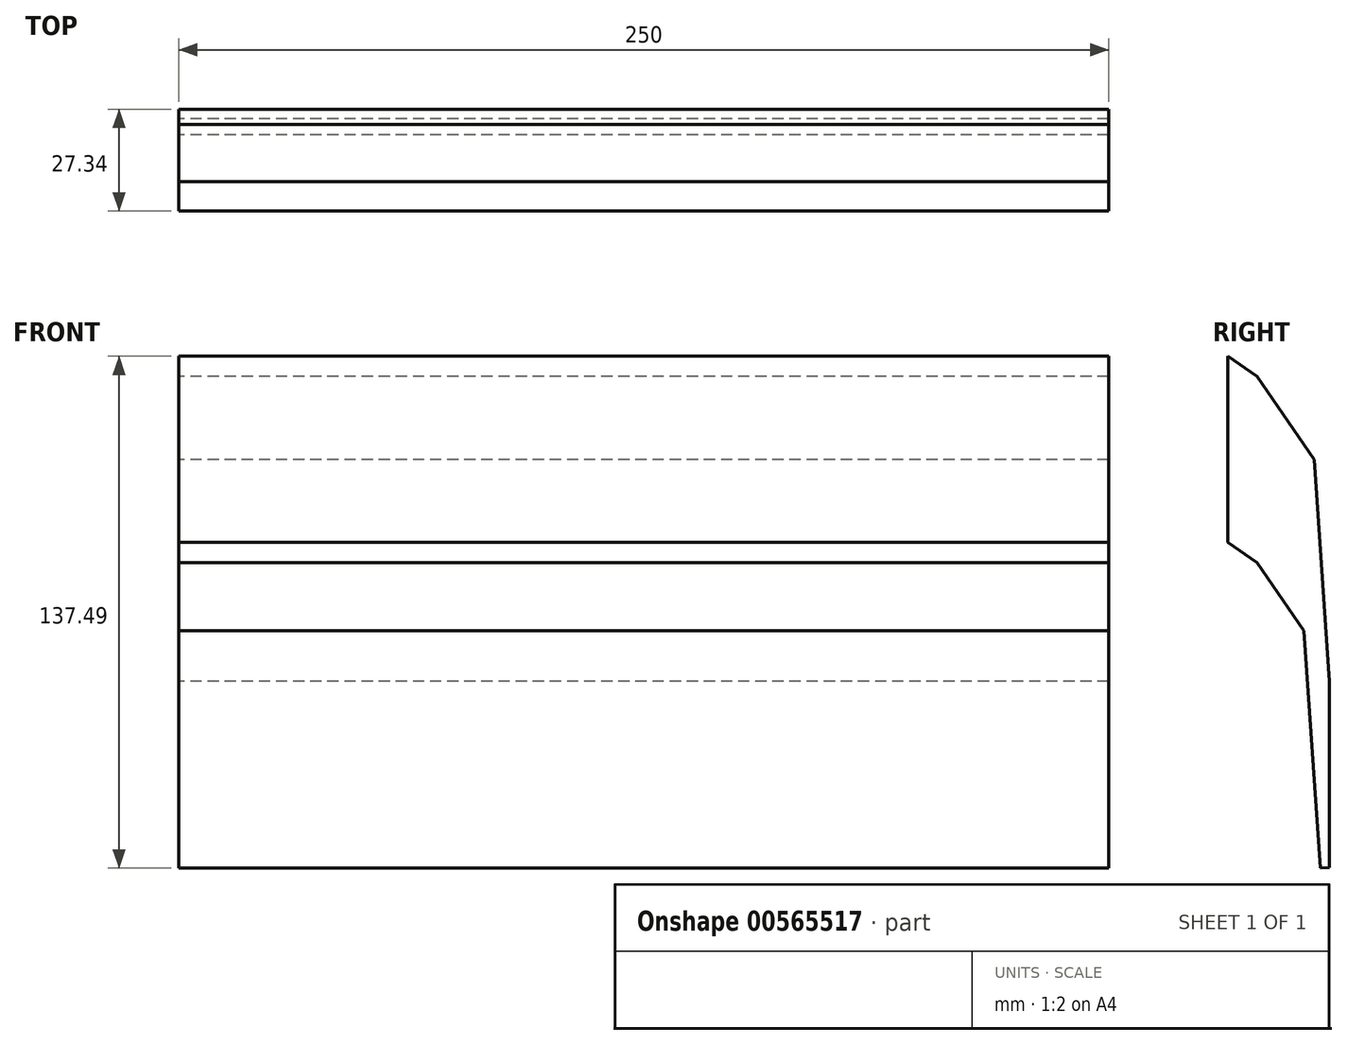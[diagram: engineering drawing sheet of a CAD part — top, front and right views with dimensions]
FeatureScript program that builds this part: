
annotation { "Feature Type Name" : "Feature", "Feature Type Description" : "" }
export const myFeature = defineFeature(function(context is Context, id is Id, definition is map)
    precondition{}
    {
        {
            var Q0;
            Q0=qCreatedBy(makeId("Front.planeOp"),FACE);
            var sketch = newSketch(context, id + "F0", { "sketchPlane" : qUnion([Q0])});
            skLineSegment(sketch, "E0.bottom", {"start": v(0, 0) * mm, "end": v(-250, 0) * mm});
            skLineSegment(sketch, "E0.top", {"start": v(0, 50) * mm, "end": v(-250, 50) * mm});
            skLineSegment(sketch, "E0.left", {"start": v(0, 0) * mm, "end": v(0, 50) * mm});
            skLineSegment(sketch, "E0.right", {"start": v(-250, 0) * mm, "end": v(-250, 50) * mm});
            skSolve(sketch);
        }
        {
            var Q0;
            Q0=qCreatedBy(makeId("Right.planeOp"),FACE);
            var sketch = newSketch(context, id + "F1", { "sketchPlane" : qUnion([Q0])});
            skLineSegment(sketch, "E1", {"start": v(0, 27.75) * mm, "end": v(-7.87, 22.34) * mm});
            skLineSegment(sketch, "E2", {"start": v(-7.87, 22.34) * mm, "end": v(-23.26, 0) * mm});
            skLineSegment(sketch, "E3", {"start": v(-23.26, 0) * mm, "end": v(-27.34, -59.57) * mm});
            skLineSegment(sketch, "E4", {"start": v(-27.34, -59.57) * mm, "end": v(-27.34, -77.25) * mm});
            skLineSegment(sketch, "E5", {"start": v(-27.34, -77.25) * mm, "end": v(15.93, -77.25) * mm});
            skLineSegment(sketch, "E6.MirrorCS", {"start": v(-27.34, -94.94) * mm, "end": v(-27.34, -77.25) * mm});
            skLineSegment(sketch, "E7.MirrorCS", {"start": v(-23.26, -154.5) * mm, "end": v(-27.34, -94.94) * mm});
            skLineSegment(sketch, "E8.MirrorCS", {"start": v(-7.87, -176.85) * mm, "end": v(-23.26, -154.5) * mm});
            skLineSegment(sketch, "E9.MirrorCS", {"start": v(0, -182.25) * mm, "end": v(-7.87, -176.85) * mm});
            skLineSegment(sketch, "E10.MirrorCS", {"start": v(0, 27.75) * mm, "end": v(7.87, 22.34) * mm});
            skLineSegment(sketch, "E11.MirrorCS", {"start": v(7.87, 22.34) * mm, "end": v(23.26, 0) * mm});
            skLineSegment(sketch, "E12.MirrorCS", {"start": v(23.26, 0) * mm, "end": v(27.34, -59.57) * mm});
            skLineSegment(sketch, "E13.MirrorCS", {"start": v(27.34, -94.94) * mm, "end": v(27.34, -77.25) * mm});
            skLineSegment(sketch, "E14.MirrorCS", {"start": v(27.34, -59.57) * mm, "end": v(27.34, -77.25) * mm});
            skLineSegment(sketch, "E15.MirrorCS", {"start": v(0, -182.25) * mm, "end": v(7.87, -176.85) * mm});
            skLineSegment(sketch, "E16.MirrorCS", {"start": v(7.87, -176.85) * mm, "end": v(23.26, -154.5) * mm});
            skLineSegment(sketch, "E17.MirrorCS", {"start": v(23.26, -154.5) * mm, "end": v(27.34, -94.94) * mm});
            skSolve(sketch);
        }
        {
            var Q0;
            Q0=makeQuery(id+"F0.imprint","IMPRINT",FACE,{"disambiguationData":[TD([[makeQuery(id+"F0.imprint","IMPRINT",EDGE,{"derivedFrom":sQuery(id+"F0.wireOp",EDGE,"E0.bottom")}),-1.0]])]});
            var Q1;
            Q1=sQuery(id+"F1.wireOp",EDGE,"E10.MirrorCS");
            sweep(context, id + "F2", {"profiles" : qUnion([Q0]), "path" : qUnion([Q1])});
        }
        {
            var Q0;
            Q0=makeQuery(id+"F2.opSweep","CAP_FACE",FACE,{"disambiguationData":[OSD([sQuery(id+"F0.wireOp",EDGE,"E0.bottom"),sQuery(id+"F0.wireOp",EDGE,"E0.top"),sQuery(id+"F0.wireOp",EDGE,"E0.left"),sQuery(id+"F0.wireOp",EDGE,"E0.right"),sQuery(id+"F1.wireOp",VERTEX,"E10.MirrorCS.end")])],"isStart":false});
            var Q1;
            Q1=sQuery(id+"F1.wireOp",EDGE,"E11.MirrorCS");
            sweep(context, id + "F3", {"operationType" : NewBodyOperationType.ADD, "profiles" : qUnion([Q0]), "path" : qUnion([Q1])});
        }
        {
            var Q0;
            Q0=makeQuery(id+"F3.opSweep","CAP_FACE",FACE,{"disambiguationData":[OSD([sQuery(id+"F0.wireOp",EDGE,"E0.bottom"),sQuery(id+"F0.wireOp",EDGE,"E0.top"),sQuery(id+"F0.wireOp",EDGE,"E0.left"),sQuery(id+"F0.wireOp",EDGE,"E0.right"),sQuery(id+"F1.wireOp",VERTEX,"E10.MirrorCS.end"),sQuery(id+"F1.wireOp",VERTEX,"E11.MirrorCS.end")])],"isStart":false});
            var Q1;
            Q1=sQuery(id+"F1.wireOp",EDGE,"E12.MirrorCS");
            sweep(context, id + "F4", {"operationType" : NewBodyOperationType.ADD, "profiles" : qUnion([Q0]), "path" : qUnion([Q1])});
        }
        {
            var Q0;
            Q0=makeQuery(id+"F4.opSweep","SWEPT_FACE",FACE,{"disambiguationData":[OSD([sQuery(id+"F0.wireOp",EDGE,"E0.bottom"),sQuery(id+"F1.wireOp",VERTEX,"E10.MirrorCS.end"),sQuery(id+"F1.wireOp",VERTEX,"E11.MirrorCS.end"),sQuery(id+"F1.wireOp",EDGE,"E12.MirrorCS")])]});
            extrude(context, id + "F5", {"entities" : qUnion([Q0]), "operationType" : NewBodyOperationType.ADD, "depth" : 2.5 * mm, "offsetDistance" : 25 * mm});
        }
        {
            var Q0;
            Q0=makeQuery(id+"F5.opExtrude","SWEPT_FACE",FACE,{"disambiguationData":[OSD([sQuery(id+"F0.wireOp",EDGE,"E0.bottom"),sQuery(id+"F1.wireOp",VERTEX,"E10.MirrorCS.end"),sQuery(id+"F1.wireOp",VERTEX,"E11.MirrorCS.end"),sQuery(id+"F1.wireOp",VERTEX,"E12.MirrorCS.start")])]});
            extrude(context, id + "F6", {"entities" : qUnion([Q0]), "operationType" : NewBodyOperationType.ADD, "depth" : 25 * mm, "offsetDistance" : 25 * mm});
        }
    });
